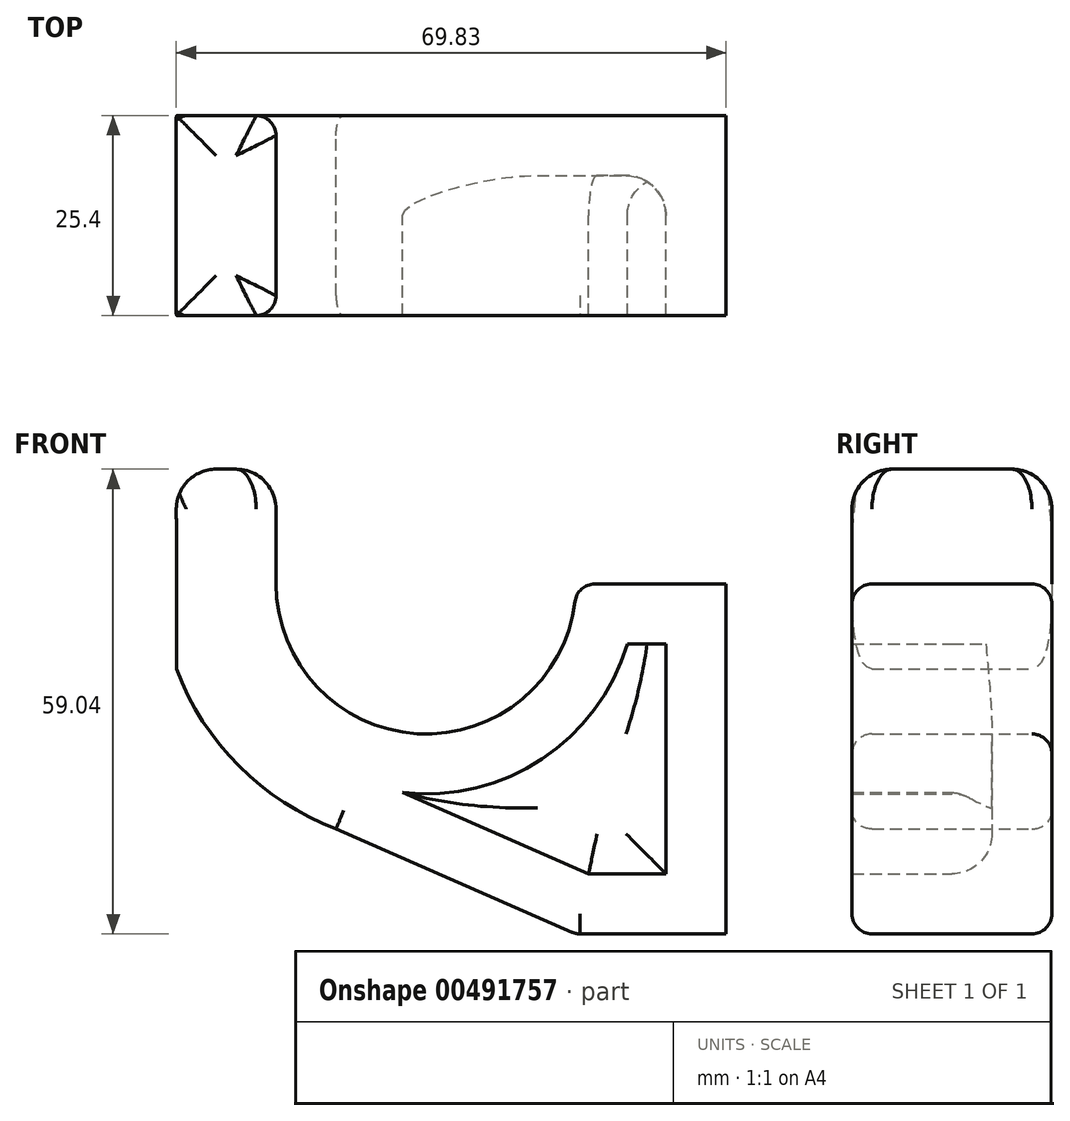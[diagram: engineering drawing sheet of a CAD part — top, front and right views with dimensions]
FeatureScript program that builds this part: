
annotation { "Feature Type Name" : "Feature", "Feature Type Description" : "" }
export const myFeature = defineFeature(function(context is Context, id is Id, definition is map)
    precondition{}
    {
        {
            var Q0;
            Q0=qCreatedBy(makeId("Front.planeOp"),FACE);
            var sketch = newSketch(context, id + "F0", { "sketchPlane" : qUnion([Q0])});
            skLineSegment(sketch, "E0", {"start": v(-15.24, 12.16) * mm, "end": v(-15.24, -32.3) * mm});
            skLineSegment(sketch, "E1", {"start": v(-15.24, -32.3) * mm, "end": v(-34.3, -32.3) * mm});
            skArc(sketch, "E2", {"start": v(-72.4, 12.16) * mm, "mid": v(-53.34, -6.9) * mm, "end": v(-34.3, 12.16) * mm});
            skLineSegment(sketch, "E3", {"start": v(-34.3, 12.16) * mm, "end": v(-15.24, 12.16) * mm});
            skLineSegment(sketch, "E4.top", {"start": v(-72.4, 26.75) * mm, "end": v(-85.1, 26.75) * mm});
            skLineSegment(sketch, "E4.left", {"start": v(-72.4, 12.16) * mm, "end": v(-72.4, 26.75) * mm});
            skArc(sketch, "E5", {"start": v(-85.05, 1.35) * mm, "mid": v(-77.09, -10.99) * mm, "end": v(-64.77, -18.97) * mm});
            skLineSegment(sketch, "E6", {"start": v(-64.77, -18.97) * mm, "end": v(-34.3, -32.3) * mm});
            skLineSegment(sketch, "E7", {"start": v(-85.1, 26.75) * mm, "end": v(-85.05, 16.59) * mm});
            skLineSegment(sketch, "E8", {"start": v(-85.05, 16.59) * mm, "end": v(-85.05, 1.35) * mm});
            skSolve(sketch);
        }
        {
            var Q0;
            Q0=qSketchRegion(id+"F0",true);
            extrude(context, id + "F1", {"entities" : qUnion([Q0]), "depth" : 25.4 * mm});
        }
        {
            var Q0;
            Q0=makeQuery(id+"F1.opExtrude","CAP_FACE",FACE,{"disambiguationData":[OSD([sQuery(id+"F0.wireOp",EDGE,"E0"),sQuery(id+"F0.wireOp",EDGE,"E1"),sQuery(id+"F0.wireOp",EDGE,"AQg3ZOSh-IiF6-WGtp-ymMu-zU6TPKDDiS5l"),sQuery(id+"F0.wireOp",EDGE,"E2"),sQuery(id+"F0.wireOp",EDGE,"E3"),sQuery(id+"F0.wireOp",EDGE,"E4.top"),sQuery(id+"F0.wireOp",EDGE,"E4.left"),sQuery(id+"F0.wireOp",EDGE,"E4.right"),sQuery(id+"F0.wireOp",EDGE,"E5"),sQuery(id+"F0.wireOp",EDGE,"E6")])],"isStart":false});
            shell(context, id + "F2", {"entities" : qUnion([Q0]), "thickness" : 7.62 * mm});
        }
        {
            var Q0;
            Q0=makeQuery(id+"F2.opShell","OFFSET_FACE",FACE,{"disambiguationData":[OSD([sQuery(id+"F0.wireOp",EDGE,"E0"),sQuery(id+"F0.wireOp",EDGE,"E1"),sQuery(id+"F0.wireOp",EDGE,"AQg3ZOSh-IiF6-WGtp-ymMu-zU6TPKDDiS5l"),sQuery(id+"F0.wireOp",EDGE,"E2"),sQuery(id+"F0.wireOp",EDGE,"E3"),sQuery(id+"F0.wireOp",EDGE,"E4.top"),sQuery(id+"F0.wireOp",EDGE,"E4.left"),sQuery(id+"F0.wireOp",EDGE,"E4.right"),sQuery(id+"F0.wireOp",EDGE,"E5"),sQuery(id+"F0.wireOp",EDGE,"E6")])]});
            fillet(context, id + "F3", {"entities" : qUnion([Q0]), "radius" : 5.08 * mm, "tangentPropagation" : true, "allowEdgeOverflow" : false});
        }
        {
            var Q0;
            Q0=makeQuery(id+"F1.opExtrude","SWEPT_FACE",FACE,{"disambiguationData":[OSD([sQuery(id+"F0.wireOp",EDGE,"E4.top")])]});
            fillet(context, id + "F4", {"entities" : qUnion([Q0]), "radius" : 5.08 * mm, "tangentPropagation" : true, "allowEdgeOverflow" : false});
        }
        {
            var Q0;
            Q0=makeQuery(id+"F1.opExtrude","CAP_EDGE",EDGE,{"disambiguationData":[OSD([sQuery(id+"F0.wireOp",EDGE,"E3")])],"isStart":false});
            fillet(context, id + "F5", {"entities" : qUnion([Q0]), "radius" : 2.54 * mm, "tangentPropagation" : true, "allowEdgeOverflow" : false});
        }
        {
            var Q0;
            Q0=makeQuery(id+"F1.opExtrude","CAP_EDGE",EDGE,{"disambiguationData":[OSD([sQuery(id+"F0.wireOp",EDGE,"E3")])],"isStart":true});
            fillet(context, id + "F6", {"entities" : qUnion([Q0]), "radius" : 2.54 * mm, "tangentPropagation" : true, "allowEdgeOverflow" : false});
        }
        {
            var Q0;
            Q0=makeQuery(id+"F1.opExtrude","CAP_EDGE",EDGE,{"disambiguationData":[OSD([sQuery(id+"F0.wireOp",EDGE,"E1")])],"isStart":false});
            fillet(context, id + "F7", {"entities" : qUnion([Q0]), "radius" : 2.54 * mm, "tangentPropagation" : true, "allowEdgeOverflow" : false});
        }
        {
            var Q0;
            Q0=makeQuery(id+"F1.opExtrude","CAP_EDGE",EDGE,{"disambiguationData":[OSD([sQuery(id+"F0.wireOp",EDGE,"E6")])],"isStart":false});
            fillet(context, id + "F8", {"entities" : qUnion([Q0]), "radius" : 2.54 * mm, "tangentPropagation" : true, "allowEdgeOverflow" : false});
        }
        {
            var Q0;
            Q0=makeQuery(id+"F1.opExtrude","SWEPT_EDGE",EDGE,{"disambiguationData":[OSD([sQuery(id+"F0.wireOp",EDGE,"E2"),sQuery(id+"F0.wireOp",EDGE,"E3")])]});
            var Q1;
            Q1=makeQuery(id+"F1.opExtrude","CAP_EDGE",EDGE,{"disambiguationData":[OSD([sQuery(id+"F0.wireOp",EDGE,"E4.right")])],"isStart":false});
            var Q2;
            Q2=makeQuery(id+"F1.opExtrude","CAP_EDGE",EDGE,{"disambiguationData":[OSD([sQuery(id+"F0.wireOp",EDGE,"AQg3ZOSh-IiF6-WGtp-ymMu-zU6TPKDDiS5l")])],"isStart":false});
            var Q3;
            Q3=makeQuery(id+"F1.opExtrude","CAP_EDGE",EDGE,{"disambiguationData":[OSD([sQuery(id+"F0.wireOp",EDGE,"E5")])],"isStart":false});
            fillet(context, id + "F9", {"entities" : qUnion([Q0, Q1, Q2, Q3]), "radius" : 2.54 * mm, "tangentPropagation" : true, "allowEdgeOverflow" : false});
        }
        {
            var Q0;
            Q0=makeQuery(id+"F1.opExtrude","CAP_EDGE",EDGE,{"disambiguationData":[OSD([sQuery(id+"F0.wireOp",EDGE,"E1")])],"isStart":true});
            var Q1;
            Q1=makeQuery(id+"F1.opExtrude","CAP_EDGE",EDGE,{"disambiguationData":[OSD([sQuery(id+"F0.wireOp",EDGE,"E6")])],"isStart":true});
            var Q2;
            Q2=makeQuery(id+"F1.opExtrude","CAP_EDGE",EDGE,{"disambiguationData":[OSD([sQuery(id+"F0.wireOp",EDGE,"AQg3ZOSh-IiF6-WGtp-ymMu-zU6TPKDDiS5l")])],"isStart":true});
            fillet(context, id + "F10", {"entities" : qUnion([Q0, Q1, Q2]), "radius" : 2.54 * mm, "tangentPropagation" : true, "allowEdgeOverflow" : false});
        }
        {
            var Q0;
            Q0=makeQuery(id+"F1.opExtrude","CAP_EDGE",EDGE,{"disambiguationData":[OSD([sQuery(id+"F0.wireOp",EDGE,"E5")])],"isStart":true});
            fillet(context, id + "F11", {"entities" : qUnion([Q0]), "radius" : 2.54 * mm, "tangentPropagation" : true, "allowEdgeOverflow" : false});
        }
    });
